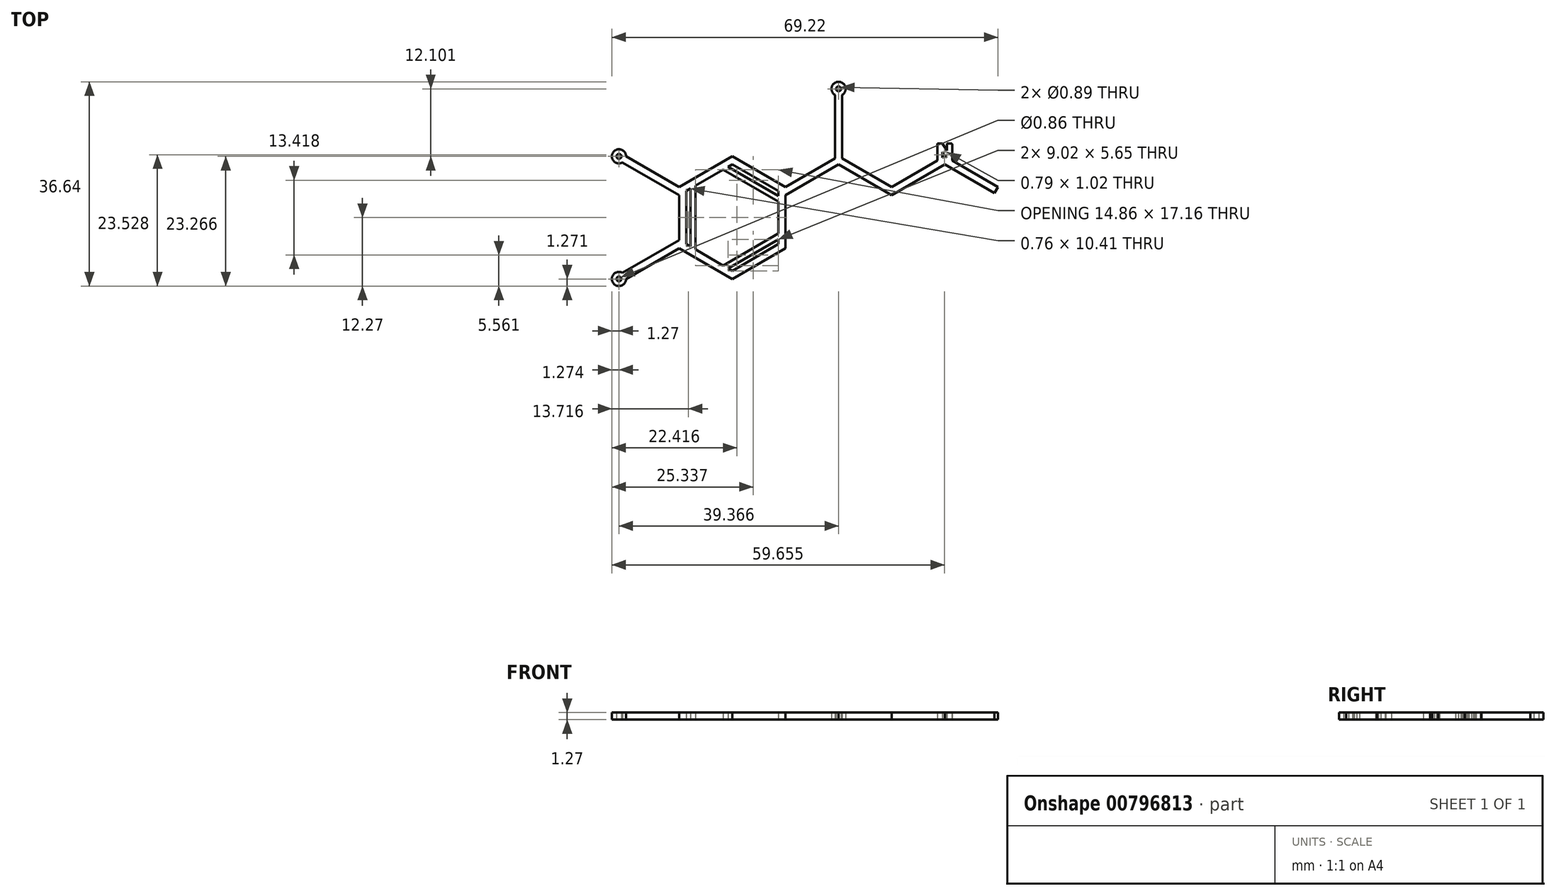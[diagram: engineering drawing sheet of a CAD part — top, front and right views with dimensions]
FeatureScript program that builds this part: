
annotation { "Feature Type Name" : "Feature", "Feature Type Description" : "" }
export const myFeature = defineFeature(function(context is Context, id is Id, definition is map)
    precondition{}
    {
        {
            var Q0;
            Q0=qCreatedBy(makeId("Top.planeOp"),FACE);
            var sketch = newSketch(context, id + "F0", { "sketchPlane" : qUnion([Q0])});
            skCircle(sketch, "E0.cCircle", {"center": v(0, 0) * mm, "radius": 9.53 * mm, "construction": true});
            skLineSegment(sketch, "E0.0", {"start": v(0, 11) * mm, "end": v(9.52, 5.5) * mm});
            skLineSegment(sketch, "E0.1", {"start": v(9.52, 4.03) * mm, "end": v(9.53, -5.5) * mm});
            skLineSegment(sketch, "E0.2", {"start": v(9.53, -5.5) * mm, "end": v(0, -11) * mm});
            skLineSegment(sketch, "E0.3", {"start": v(0, -11) * mm, "end": v(-9.52, -5.5) * mm});
            skLineSegment(sketch, "E0.4", {"start": v(-9.52, -4.03) * mm, "end": v(-9.53, 4.03) * mm});
            skLineSegment(sketch, "E0.5", {"start": v(-9.53, 5.5) * mm, "end": v(0, 11) * mm});
            skPoint(sketch, "E0.0.midPoint", {"position": v(4.76, 8.25) * mm});
            skLineSegment(sketch, "E1.0", {"start": v(-8.26, 4.77) * mm, "end": v(-7.5, 5.2) * mm});
            skLineSegment(sketch, "E1.1", {"start": v(8.25, 4.77) * mm, "end": v(8.25, 3.89) * mm});
            skLineSegment(sketch, "E1.2", {"start": v(8.26, -4.77) * mm, "end": v(0, -9.53) * mm});
            skLineSegment(sketch, "E1.3", {"start": v(0, 9.53) * mm, "end": v(8.25, 4.77) * mm});
            skLineSegment(sketch, "E1.4", {"start": v(0, -9.53) * mm, "end": v(-0.76, -9.1) * mm});
            skLineSegment(sketch, "E1.5", {"start": v(-8.25, -4.77) * mm, "end": v(-8.26, 4.77) * mm});
            skLineSegment(sketch, "E2", {"start": v(-0.76, 9.1) * mm, "end": v(8.25, 3.89) * mm});
            skLineSegment(sketch, "E3", {"start": v(8.26, -3.89) * mm, "end": v(-0.76, -9.1) * mm});
            skLineSegment(sketch, "E4", {"start": v(-7.5, -5.2) * mm, "end": v(-7.5, 5.2) * mm});
            skLineSegment(sketch, "E5", {"start": v(-6.6, 5.72) * mm, "end": v(-6.6, -5.5) * mm});
            skLineSegment(sketch, "E6", {"start": v(-1.65, 8.58) * mm, "end": v(8.25, 2.86) * mm});
            skLineSegment(sketch, "E7", {"start": v(-1.65, -8.58) * mm, "end": v(8.26, -2.86) * mm});
            skLineSegment(sketch, "E8.trimOffspring", {"start": v(-6.6, 5.72) * mm, "end": v(-1.65, 8.58) * mm});
            skLineSegment(sketch, "E9.trimOffspring", {"start": v(-0.76, 9.1) * mm, "end": v(0, 9.53) * mm});
            skLineSegment(sketch, "E10.trimOffspring", {"start": v(8.25, 2.86) * mm, "end": v(8.26, -2.86) * mm});
            skLineSegment(sketch, "E11.trimOffspring", {"start": v(8.26, -3.89) * mm, "end": v(8.26, -4.77) * mm});
            skLineSegment(sketch, "E12.trimOffspring", {"start": v(-1.65, -8.58) * mm, "end": v(-6.6, -5.72) * mm});
            skLineSegment(sketch, "E13.trimOffspring", {"start": v(-7.5, -5.2) * mm, "end": v(-8.25, -4.77) * mm});
            skLineSegment(sketch, "E14", {"start": v(-6.6, -5.72) * mm, "end": v(-6.6, -5.5) * mm});
            skLineSegment(sketch, "E15", {"start": v(-8.25, 0) * mm, "end": v(-7.5, 0) * mm});
            skLineSegment(sketch, "E16", {"start": v(9.52, 5.5) * mm, "end": v(18.42, 10.63) * mm});
            skLineSegment(sketch, "E17", {"start": v(18.42, 11) * mm, "end": v(18.42, 22) * mm});
            skLineSegment(sketch, "E18", {"start": v(-9.53, 5.5) * mm, "end": v(-19.05, 11) * mm});
            skLineSegment(sketch, "E19", {"start": v(-9.52, -5.5) * mm, "end": v(-19.05, -11) * mm});
            skLineSegment(sketch, "E20.0", {"start": v(-9.53, 4.03) * mm, "end": v(-19.68, 9.9) * mm});
            skLineSegment(sketch, "E21.0", {"start": v(-9.52, -4.03) * mm, "end": v(-19.69, -9.9) * mm});
            skLineSegment(sketch, "E22.0", {"start": v(38.1, 9.53) * mm, "end": v(47, 4.4) * mm});
            skLineSegment(sketch, "E22.1", {"start": v(28.58, 4.03) * mm, "end": v(38.1, 9.53) * mm});
            skLineSegment(sketch, "E22.2", {"start": v(19.05, 9.53) * mm, "end": v(28.58, 4.03) * mm});
            skLineSegment(sketch, "E22.3", {"start": v(9.52, 4.03) * mm, "end": v(19.05, 9.53) * mm});
            skLineSegment(sketch, "E23", {"start": v(47.63, 5.5) * mm, "end": v(47, 4.4) * mm});
            skArc(sketch, "E24", {"start": v(-19.05, 11) * mm, "mid": v(-21.42, 11.63) * mm, "end": v(-19.68, 9.9) * mm});
            skCircle(sketch, "E25", {"center": v(-20.32, 11) * mm, "radius": 0.44 * mm});
            skLineSegment(sketch, "E26.0", {"start": v(19.69, 11) * mm, "end": v(19.69, 22) * mm});
            skLineSegment(sketch, "E27", {"start": v(18.42, 11) * mm, "end": v(18.42, 10.63) * mm});
            skLineSegment(sketch, "E28", {"start": v(19.69, 10.63) * mm, "end": v(19.69, 11) * mm});
            skLineSegment(sketch, "E29.trimOffspring", {"start": v(19.69, 10.63) * mm, "end": v(28.58, 5.5) * mm});
            skPoint(sketch, "E30.orphan", {"position": v(18.42, 11) * mm});
            skArc(sketch, "E31", {"start": v(19.69, 22) * mm, "mid": v(19.05, 24.37) * mm, "end": v(18.42, 22) * mm});
            skCircle(sketch, "E32", {"center": v(19.05, 23.1) * mm, "radius": 0.44 * mm});
            skArc(sketch, "E33", {"start": v(-19.69, -9.9) * mm, "mid": v(-21.42, -11.63) * mm, "end": v(-19.05, -11) * mm});
            skCircle(sketch, "E34", {"center": v(-20.32, -11) * mm, "radius": 0.43 * mm});
            skPoint(sketch, "E35.orphan", {"position": v(38.1, 11) * mm});
            skLineSegment(sketch, "E36", {"start": v(28.58, 5.5) * mm, "end": v(38.1, 11) * mm});
            skLineSegment(sketch, "E37", {"start": v(47.63, 5.5) * mm, "end": v(38.1, 11) * mm});
            skLineSegment(sketch, "E38.left", {"start": v(36.76, 13.27) * mm, "end": v(36.76, 10.73) * mm});
            skLineSegment(sketch, "E38.right", {"start": v(37.65, 11.86) * mm, "end": v(37.65, 10.73) * mm});
            skLineSegment(sketch, "E39", {"start": v(36.76, 13.27) * mm, "end": v(37.65, 13.27) * mm});
            skLineSegment(sketch, "E40", {"start": v(37.65, 13.27) * mm, "end": v(38.51, 12.04) * mm});
            skLineSegment(sketch, "E41", {"start": v(38.51, 12.04) * mm, "end": v(38.51, 13.27) * mm});
            skLineSegment(sketch, "E42", {"start": v(38.51, 13.27) * mm, "end": v(39.4, 13.27) * mm});
            skLineSegment(sketch, "E43", {"start": v(39.4, 13.27) * mm, "end": v(39.4, 10.73) * mm});
            skLineSegment(sketch, "E44", {"start": v(37.65, 11.86) * mm, "end": v(38.57, 10.73) * mm});
            skLineSegment(sketch, "E45", {"start": v(36.76, 10.73) * mm, "end": v(36.76, 10.22) * mm});
            skLineSegment(sketch, "E46", {"start": v(36.76, 10.22) * mm, "end": v(37.65, 10.73) * mm});
            skLineSegment(sketch, "E47", {"start": v(38.57, 10.73) * mm, "end": v(39.4, 10.22) * mm});
            skLineSegment(sketch, "E48", {"start": v(39.4, 10.22) * mm, "end": v(39.4, 10.73) * mm});
            skSolve(sketch);
        }
        {
            var Q0;
            Q0 = qSketchRegion(id + "F0", true);
            extrude(context, id + "F1", {"entities" : qUnion([Q0]), "depth" : 1.27 * mm, "offsetDistance" : 25.4 * mm});
        }
        {
            var Q0;
            Q0=qCreatedBy(makeId("Top.planeOp"),FACE);
            var sketch = newSketch(context, id + "F2", { "sketchPlane" : qUnion([Q0])});
            skLineSegment(sketch, "E49.left", {"start": v(36.78, 13.18) * mm, "end": v(36.78, 10.64) * mm});
            skLineSegment(sketch, "E49.right", {"start": v(37.67, 11.77) * mm, "end": v(37.67, 10.64) * mm});
            skLineSegment(sketch, "E50", {"start": v(36.78, 13.18) * mm, "end": v(37.67, 13.18) * mm});
            skLineSegment(sketch, "E51", {"start": v(37.67, 13.18) * mm, "end": v(38.53, 11.95) * mm});
            skLineSegment(sketch, "E52", {"start": v(38.53, 11.95) * mm, "end": v(38.53, 13.18) * mm});
            skLineSegment(sketch, "E53", {"start": v(38.53, 13.18) * mm, "end": v(39.42, 13.18) * mm});
            skLineSegment(sketch, "E54", {"start": v(39.42, 13.18) * mm, "end": v(39.42, 10.64) * mm});
            skLineSegment(sketch, "E55", {"start": v(37.67, 11.77) * mm, "end": v(38.59, 10.64) * mm});
            skLineSegment(sketch, "E56", {"start": v(36.78, 10.64) * mm, "end": v(36.78, 10.13) * mm});
            skLineSegment(sketch, "E57", {"start": v(36.78, 10.13) * mm, "end": v(37.67, 10.64) * mm});
            skLineSegment(sketch, "E58", {"start": v(38.59, 10.64) * mm, "end": v(39.42, 10.13) * mm});
            skLineSegment(sketch, "E59", {"start": v(39.42, 10.13) * mm, "end": v(39.42, 10.64) * mm});
            skSolve(sketch);
        }
        {
            var Q0;
            Q0 = qSketchRegion(id + "F2", true);
            var Q1;
            Q1=sQuery(id+"F2.wireOp",EDGE,"E55");
            var Q2;
            Q2=sQuery(id+"F2.wireOp",EDGE,"E54");
            var Q3;
            Q3=sQuery(id+"F2.wireOp",EDGE,"E49.left");
            var Q4;
            Q4=sQuery(id+"F2.wireOp",EDGE,"E56");
            var Q5;
            Q5=sQuery(id+"F2.wireOp",EDGE,"E49.right");
            var Q6;
            Q6=sQuery(id+"F2.wireOp",EDGE,"E51");
            var Q7;
            Q7=sQuery(id+"F2.wireOp",EDGE,"E57");
            var Q8;
            Q8=sQuery(id+"F2.wireOp",EDGE,"E52");
            var Q9;
            Q9=sQuery(id+"F2.wireOp",EDGE,"E53");
            var Q10;
            Q10=sQuery(id+"F2.wireOp",EDGE,"E50");
            var Q11;
            Q11=sQuery(id+"F2.wireOp",EDGE,"E58");
            var Q12;
            Q12=sQuery(id+"F2.wireOp",EDGE,"E59");
            var Q13;
            Q13=makeQuery(id+"F1.opExtrude","SWEPT_BODY",BODY,{"disambiguationData":[OSD([sQuery(id+"F0.wireOp",EDGE,"E0.0"),sQuery(id+"F0.wireOp",EDGE,"E0.1"),sQuery(id+"F0.wireOp",EDGE,"E0.2"),sQuery(id+"F0.wireOp",EDGE,"E0.3"),sQuery(id+"F0.wireOp",EDGE,"E0.4"),sQuery(id+"F0.wireOp",EDGE,"E0.5"),sQuery(id+"F0.wireOp",EDGE,"E1.0"),sQuery(id+"F0.wireOp",EDGE,"E1.1"),sQuery(id+"F0.wireOp",EDGE,"E1.2"),sQuery(id+"F0.wireOp",EDGE,"E1.3"),sQuery(id+"F0.wireOp",EDGE,"E1.4"),sQuery(id+"F0.wireOp",EDGE,"E1.5"),sQuery(id+"F0.wireOp",EDGE,"E2"),sQuery(id+"F0.wireOp",EDGE,"E3"),sQuery(id+"F0.wireOp",EDGE,"E4"),sQuery(id+"F0.wireOp",EDGE,"E5"),sQuery(id+"F0.wireOp",EDGE,"E6"),sQuery(id+"F0.wireOp",EDGE,"E7"),sQuery(id+"F0.wireOp",EDGE,"E8.trimOffspring"),sQuery(id+"F0.wireOp",EDGE,"E9.trimOffspring"),sQuery(id+"F0.wireOp",EDGE,"E10.trimOffspring"),sQuery(id+"F0.wireOp",EDGE,"E11.trimOffspring"),sQuery(id+"F0.wireOp",EDGE,"E12.trimOffspring"),sQuery(id+"F0.wireOp",EDGE,"E13.trimOffspring"),sQuery(id+"F0.wireOp",EDGE,"E14"),sQuery(id+"F0.wireOp",EDGE,"E16"),sQuery(id+"F0.wireOp",EDGE,"E17"),sQuery(id+"F0.wireOp",EDGE,"E18"),sQuery(id+"F0.wireOp",EDGE,"E19"),sQuery(id+"F0.wireOp",EDGE,"E20.0"),sQuery(id+"F0.wireOp",EDGE,"E21.0"),sQuery(id+"F0.wireOp",EDGE,"E22.0"),sQuery(id+"F0.wireOp",EDGE,"E22.1"),sQuery(id+"F0.wireOp",EDGE,"E22.2"),sQuery(id+"F0.wireOp",EDGE,"E22.3"),sQuery(id+"F0.wireOp",EDGE,"E23"),sQuery(id+"F0.wireOp",EDGE,"E24"),sQuery(id+"F0.wireOp",EDGE,"E25"),sQuery(id+"F0.wireOp",EDGE,"E26.0"),sQuery(id+"F0.wireOp",EDGE,"E27"),sQuery(id+"F0.wireOp",EDGE,"E28"),sQuery(id+"F0.wireOp",EDGE,"E29.trimOffspring"),sQuery(id+"F0.wireOp",EDGE,"E31"),sQuery(id+"F0.wireOp",EDGE,"E32"),sQuery(id+"F0.wireOp",EDGE,"E33"),sQuery(id+"F0.wireOp",EDGE,"E34"),sQuery(id+"F0.wireOp",EDGE,"E36"),sQuery(id+"F0.wireOp",EDGE,"E37")])]});
            extrude(context, id + "F3", {"entities" : qUnion([Q0]), "operationType" : NewBodyOperationType.ADD, "surfaceOperationType" : NewSurfaceOperationType.ADD, "surfaceEntities" : qUnion([Q1, Q2, Q3, Q4, Q5, Q6, Q7, Q8, Q9, Q10, Q11, Q12]), "depth" : 1.27 * mm, "endBoundEntityBody" : qUnion([Q13]), "offsetDistance" : 25.4 * mm});
        }
    });
